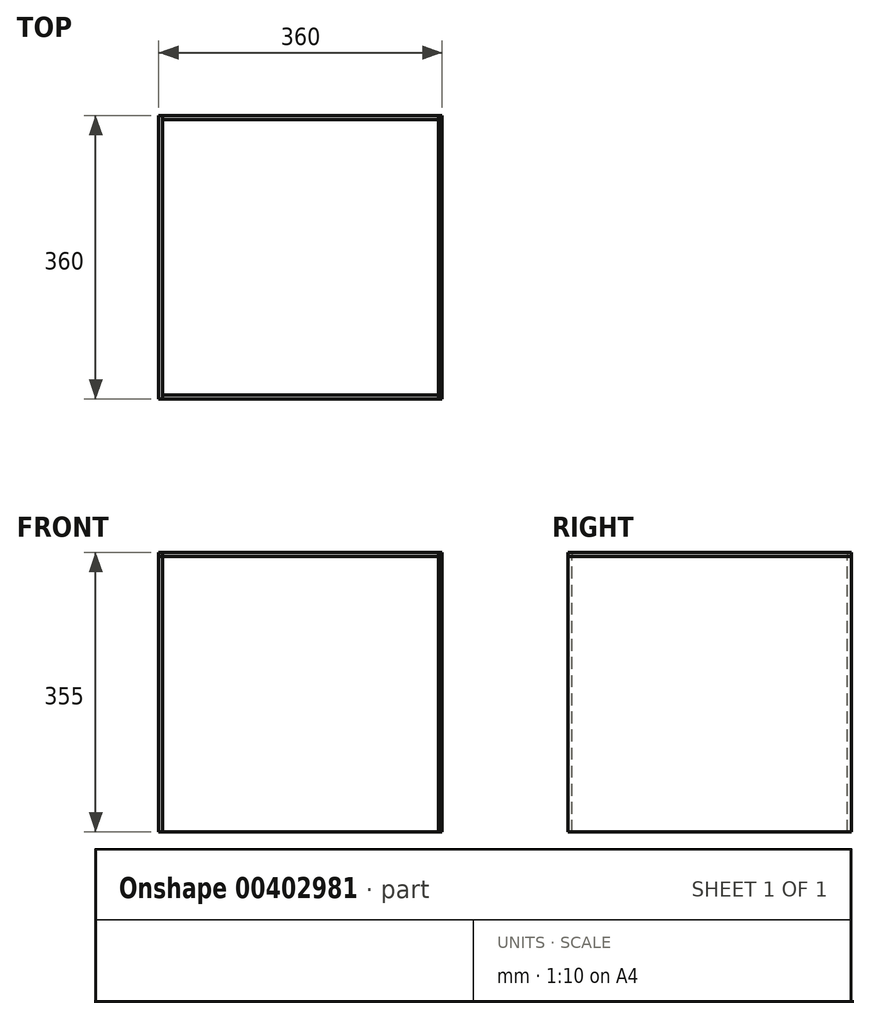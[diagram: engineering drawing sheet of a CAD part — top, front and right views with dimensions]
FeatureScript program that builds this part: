
annotation { "Feature Type Name" : "Feature", "Feature Type Description" : "" }
export const myFeature = defineFeature(function(context is Context, id is Id, definition is map)
    precondition{}
    {
        {
            assignVariable(context, id + "F0", {"name" : "material_thickness", "anyValue" : 5});
        }
        {
            var Q0;
            Q0=qCreatedBy(makeId("Top.planeOp"),FACE);
            var sketch = newSketch(context, id + "F1", { "sketchPlane" : qUnion([Q0])});
            skLineSegment(sketch, "E0.bottom", {"start": v(0, 0) * mm, "end": v(350, 0) * mm});
            skLineSegment(sketch, "E0.top", {"start": v(0, 350) * mm, "end": v(350, 350) * mm});
            skLineSegment(sketch, "E0.left", {"start": v(0, 0) * mm, "end": v(0, 350) * mm});
            skLineSegment(sketch, "E0.right", {"start": v(350, 0) * mm, "end": v(350, 350) * mm});
            skSolve(sketch);
        }
        {
            var Q0;
            Q0=qCreatedBy(makeId("Right.planeOp"),FACE);
            var sketch = newSketch(context, id + "F2", { "sketchPlane" : qUnion([Q0])});
            skLineSegment(sketch, "E1.bottom", {"start": v(0, 0) * mm, "end": v(350, 0) * mm});
            skLineSegment(sketch, "E1.top", {"start": v(0, 350) * mm, "end": v(350, 350) * mm});
            skLineSegment(sketch, "E1.left", {"start": v(0, 0) * mm, "end": v(0, 350) * mm});
            skLineSegment(sketch, "E1.right", {"start": v(350, 0) * mm, "end": v(350, 350) * mm});
            skSolve(sketch);
        }
        {
            var Q0;
            Q0=qCreatedBy(makeId("Front.planeOp"),FACE);
            var sketch = newSketch(context, id + "F3", { "sketchPlane" : qUnion([Q0])});
            skLineSegment(sketch, "E2.bottom", {"start": v(0, 0) * mm, "end": v(350, 0) * mm});
            skLineSegment(sketch, "E2.top", {"start": v(0, 350) * mm, "end": v(350, 350) * mm});
            skLineSegment(sketch, "E2.left", {"start": v(0, 0) * mm, "end": v(0, 350) * mm});
            skLineSegment(sketch, "E2.right", {"start": v(350, 0) * mm, "end": v(350, 350) * mm});
            skSolve(sketch);
        }
        {
            var Q0;
            Q0=sQuery(id+"F2.wireOp",VERTEX,"E1.right.start");
            var Q1;
            Q1=sQuery(id+"F1.wireOp",VERTEX,"E0.right.end");
            var Q2;
            Q2=sQuery(id+"F2.wireOp",VERTEX,"E1.right.end");
            cPlane(context, id + "F4", {"entities" : qUnion([Q0, Q1, Q2]), "cplaneType" : CPlaneType.THREE_POINT, "offset" : 25 * mm, "width" : 150 * mm, "height" : 150 * mm});
        }
        {
            var Q0;
            Q0=qCreatedBy(id+"F4.planeOp",FACE);
            var sketch = newSketch(context, id + "F5", { "sketchPlane" : qUnion([Q0])});
            skLineSegment(sketch, "E3.0.0", {"start": v(-350, 350) * mm, "end": v(0, 350) * mm});
            skLineSegment(sketch, "E3.0.1", {"start": v(0, 350) * mm, "end": v(0, 0) * mm});
            skLineSegment(sketch, "E3.0.2", {"start": v(0, 0) * mm, "end": v(-350, 0) * mm});
            skLineSegment(sketch, "E3.0.3", {"start": v(-350, 0) * mm, "end": v(-350, 350) * mm});
            skSolve(sketch);
        }
        {
            var Q0;
            Q0=sQuery(id+"F1.wireOp",VERTEX,"E0.right.start");
            var Q1;
            Q1=sQuery(id+"F3.wireOp",VERTEX,"E2.right.end");
            var Q2;
            Q2=sQuery(id+"F5.wireOp",VERTEX,"E3.0.3.start");
            cPlane(context, id + "F6", {"entities" : qUnion([Q0, Q1, Q2]), "cplaneType" : CPlaneType.THREE_POINT, "offset" : 25 * mm, "width" : 150 * mm, "height" : 150 * mm});
        }
        {
            var Q0;
            Q0=qCreatedBy(id+"F6.planeOp",FACE);
            var sketch = newSketch(context, id + "F7", { "sketchPlane" : qUnion([Q0])});
            skLineSegment(sketch, "E4.0.0", {"start": v(350, 350) * mm, "end": v(0, 350) * mm});
            skLineSegment(sketch, "E4.0.1", {"start": v(0, 350) * mm, "end": v(0, 0) * mm});
            skLineSegment(sketch, "E4.0.2", {"start": v(0, 0) * mm, "end": v(350, 0) * mm});
            skLineSegment(sketch, "E4.0.3", {"start": v(350, 0) * mm, "end": v(350, 350) * mm});
            skSolve(sketch);
        }
        {
            var Q0;
            Q0=sQuery(id+"F5.wireOp",VERTEX,"E3.0.1.start");
            var Q1;
            Q1=sQuery(id+"F2.wireOp",VERTEX,"E1.left.end");
            var Q2;
            Q2=sQuery(id+"F7.wireOp",VERTEX,"E4.0.0.end");
            cPlane(context, id + "F8", {"entities" : qUnion([Q0, Q1, Q2]), "cplaneType" : CPlaneType.THREE_POINT, "offset" : 25 * mm, "width" : 150 * mm, "height" : 150 * mm});
        }
        {
            var Q0;
            Q0=qCreatedBy(id+"F8.planeOp",FACE);
            var sketch = newSketch(context, id + "F9", { "sketchPlane" : qUnion([Q0])});
            skLineSegment(sketch, "E5.0.0", {"start": v(350, -350) * mm, "end": v(0, -350) * mm});
            skLineSegment(sketch, "E5.0.1", {"start": v(0, -350) * mm, "end": v(0, 0) * mm});
            skLineSegment(sketch, "E5.0.2", {"start": v(0, 0) * mm, "end": v(350, 0) * mm});
            skLineSegment(sketch, "E5.0.3", {"start": v(350, 0) * mm, "end": v(350, -350) * mm});
            skSolve(sketch);
        }
        {
            var Q0;
            Q0=makeQuery(id+"F3.imprint","IMPRINT",FACE,{"disambiguationData":[TD([[makeQuery(id+"F3.imprint","IMPRINT",EDGE,{"derivedFrom":sQuery(id+"F3.wireOp",EDGE,"E2.bottom")}),1.0]])]});
            extrude(context, id + "F10", {"entities" : qUnion([Q0]), "depth" : getVariable(context, 'material_thickness') * mm});
        }
        {
            var Q0;
            Q0=makeQuery(id+"F5.imprint","IMPRINT",FACE,{"disambiguationData":[TD([[makeQuery(id+"F5.imprint","IMPRINT",EDGE,{"derivedFrom":sQuery(id+"F5.wireOp",EDGE,"E3.0.0")}),-1.0]])]});
            extrude(context, id + "F11", {"entities" : qUnion([Q0]), "depth" : getVariable(context, 'material_thickness') * mm});
        }
        {
            var Q0;
            Q0=makeQuery(id+"F10.opExtrude","SWEPT_FACE",FACE,{"disambiguationData":[OSD([sQuery(id+"F3.wireOp",EDGE,"E2.right")])]});
            var Q1;
            Q1=makeQuery(id+"F7.imprint","IMPRINT",FACE,{"disambiguationData":[TD([[makeQuery(id+"F7.imprint","IMPRINT",EDGE,{"derivedFrom":sQuery(id+"F7.wireOp",EDGE,"E4.0.0")}),1.0]])]});
            var Q2;
            Q2=makeQuery(id+"F11.opExtrude","SWEPT_FACE",FACE,{"disambiguationData":[OSD([sQuery(id+"F5.wireOp",EDGE,"E3.0.3")])]});
            extrude(context, id + "F12", {"entities" : qUnion([Q0, Q1, Q2]), "depth" : getVariable(context, 'material_thickness') * mm});
        }
        {
            var Q0;
            Q0=makeQuery(id+"F12.opExtrude","SWEPT_BODY",BODY,{"disambiguationData":[OSD([sQuery(id+"F7.wireOp",EDGE,"E4.0.0"),sQuery(id+"F7.wireOp",EDGE,"E4.0.1"),sQuery(id+"F7.wireOp",EDGE,"E4.0.2"),sQuery(id+"F7.wireOp",EDGE,"E4.0.3")])]});
            var Q1;
            Q1=makeQuery(id+"F12.opExtrude","SWEPT_BODY",BODY,{"disambiguationData":[OSD([sQuery(id+"F3.wireOp",EDGE,"E2.right")])]});
            var Q2;
            Q2=makeQuery(id+"F12.opExtrude","SWEPT_BODY",BODY,{"disambiguationData":[OSD([sQuery(id+"F5.wireOp",EDGE,"E3.0.3")])]});
            booleanBodies(context, id + "F13", {"operationType" : BooleanOperationType.UNION, "tools" : qUnion([Q0, Q1, Q2])});
        }
        {
            var Q0;
            Q0=makeQuery(id+"F2.imprint","IMPRINT",FACE,{"disambiguationData":[TD([[makeQuery(id+"F2.imprint","IMPRINT",EDGE,{"derivedFrom":sQuery(id+"F2.wireOp",EDGE,"E1.bottom")}),1.0]])]});
            var Q1;
            Q1=makeQuery(id+"F11.opExtrude","SWEPT_FACE",FACE,{"disambiguationData":[OSD([sQuery(id+"F5.wireOp",EDGE,"E3.0.1")])]});
            var Q2;
            Q2=makeQuery(id+"F10.opExtrude","SWEPT_FACE",FACE,{"disambiguationData":[OSD([sQuery(id+"F3.wireOp",EDGE,"E2.left")])]});
            extrude(context, id + "F14", {"entities" : qUnion([Q0, Q1, Q2]), "oppositeDirection" : true, "depth" : getVariable(context, 'material_thickness') * mm});
        }
        {
            var Q0;
            Q0=makeQuery(id+"F14.opExtrude","SWEPT_BODY",BODY,{"disambiguationData":[OSD([sQuery(id+"F2.wireOp",EDGE,"E1.bottom"),sQuery(id+"F2.wireOp",EDGE,"E1.top"),sQuery(id+"F2.wireOp",EDGE,"E1.left"),sQuery(id+"F2.wireOp",EDGE,"E1.right")])]});
            var Q1;
            Q1=makeQuery(id+"F14.opExtrude","SWEPT_BODY",BODY,{"disambiguationData":[OSD([sQuery(id+"F5.wireOp",EDGE,"E3.0.1")])]});
            var Q2;
            Q2=makeQuery(id+"F14.opExtrude","SWEPT_BODY",BODY,{"disambiguationData":[OSD([sQuery(id+"F3.wireOp",EDGE,"E2.left")])]});
            booleanBodies(context, id + "F15", {"operationType" : BooleanOperationType.UNION, "tools" : qUnion([Q0, Q1, Q2])});
        }
        {
            var Q0;
            Q0=makeQuery(id+"F15.opBoolean","MERGE",FACE,{"derivedFrom":[makeQuery(id+"F14.opExtrude","SWEPT_FACE",FACE,{"disambiguationData":[OSD([sQuery(id+"F2.wireOp",EDGE,"E1.top")])]}),makeQuery(id+"F14.opExtrude","SWEPT_FACE",FACE,{"disambiguationData":[OSD([sQuery(id+"F3.wireOp",EDGE,"E2.top"),sQuery(id+"F3.wireOp",EDGE,"E2.left")])]}),makeQuery(id+"F14.opExtrude","SWEPT_FACE",FACE,{"disambiguationData":[OSD([sQuery(id+"F5.wireOp",EDGE,"E3.0.0"),sQuery(id+"F5.wireOp",EDGE,"E3.0.1")])]})]});
            var Q1;
            Q1=makeQuery(id+"F9.imprint","IMPRINT",FACE,{"disambiguationData":[TD([[makeQuery(id+"F9.imprint","IMPRINT",EDGE,{"derivedFrom":sQuery(id+"F9.wireOp",EDGE,"E5.0.0")}),-1.0]])]});
            var Q2;
            Q2=makeQuery(id+"F11.opExtrude","SWEPT_FACE",FACE,{"disambiguationData":[OSD([sQuery(id+"F5.wireOp",EDGE,"E3.0.0")])]});
            var Q3;
            Q3=makeQuery(id+"F13.opBoolean","MERGE",FACE,{"derivedFrom":[makeQuery(id+"F12.opExtrude","SWEPT_FACE",FACE,{"disambiguationData":[OSD([sQuery(id+"F7.wireOp",EDGE,"E4.0.0")])]}),makeQuery(id+"F12.opExtrude","SWEPT_FACE",FACE,{"disambiguationData":[OSD([sQuery(id+"F3.wireOp",EDGE,"E2.top"),sQuery(id+"F3.wireOp",EDGE,"E2.right")])]}),makeQuery(id+"F12.opExtrude","SWEPT_FACE",FACE,{"disambiguationData":[OSD([sQuery(id+"F5.wireOp",EDGE,"E3.0.0"),sQuery(id+"F5.wireOp",EDGE,"E3.0.3")])]})]});
            var Q4;
            Q4=makeQuery(id+"F10.opExtrude","SWEPT_FACE",FACE,{"disambiguationData":[OSD([sQuery(id+"F3.wireOp",EDGE,"E2.top")])]});
            extrude(context, id + "F16", {"entities" : qUnion([Q0, Q1, Q2, Q3, Q4]), "depth" : getVariable(context, 'material_thickness') * mm});
        }
    });
